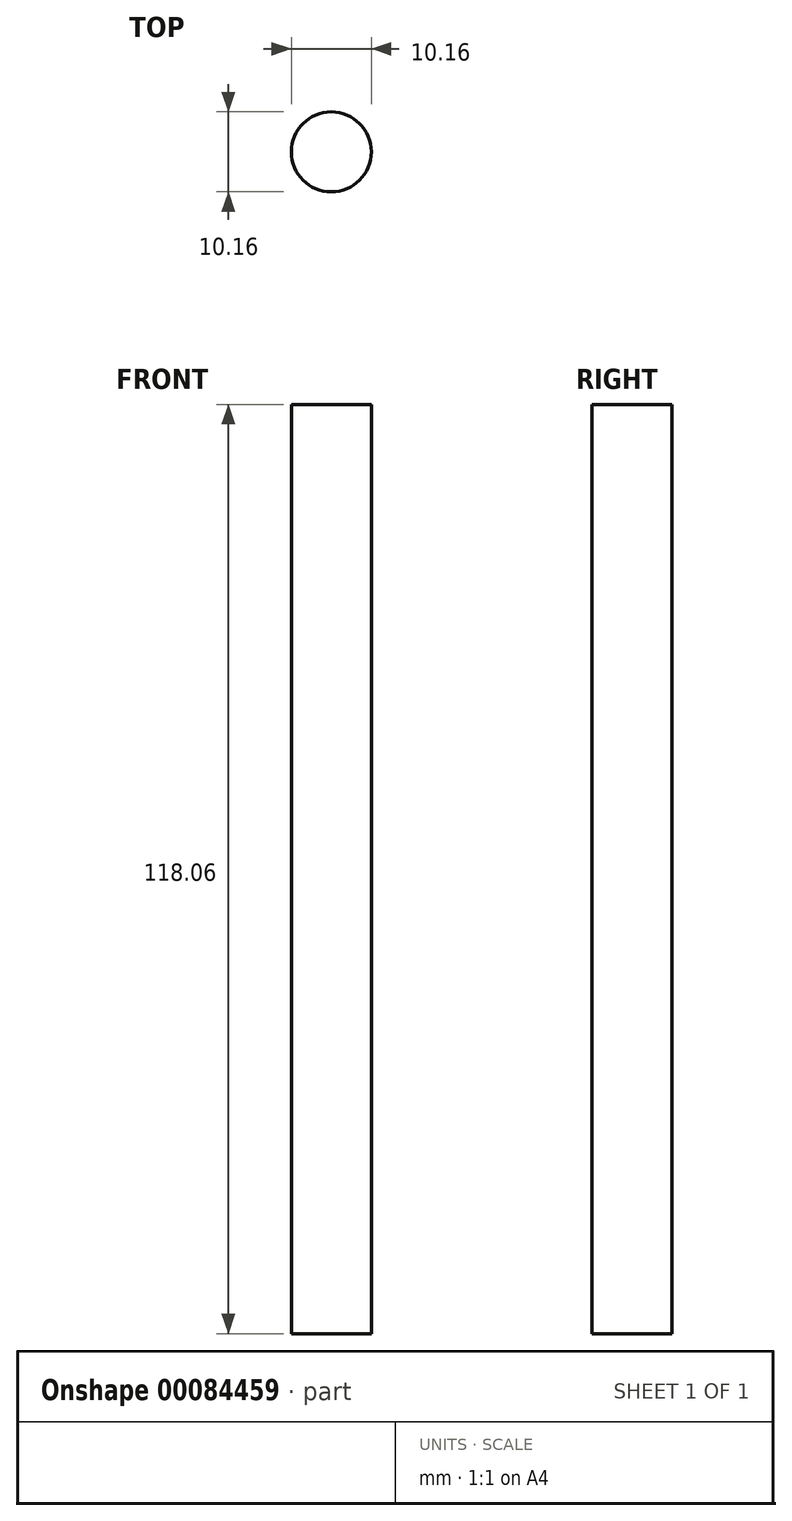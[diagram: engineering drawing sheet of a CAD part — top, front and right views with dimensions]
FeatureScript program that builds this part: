
annotation { "Feature Type Name" : "Feature", "Feature Type Description" : "" }
export const myFeature = defineFeature(function(context is Context, id is Id, definition is map)
    precondition{}
    {
        {
            var Q0;
            Q0=qCreatedBy(makeId("Top.planeOp"),FACE);
            var sketch = newSketch(context, id + "F0", { "sketchPlane" : qUnion([Q0])});
            skCircle(sketch, "E0", {"center": v(0, 0) * mm, "radius": 5.08 * mm});
            skSolve(sketch);
        }
        {
            var Q0;
            Q0=makeQuery(id+"F0.imprint","IMPRINT",FACE,{"disambiguationData":[TD([[makeQuery(id+"F0.imprint","IMPRINT",EDGE,{"derivedFrom":sQuery(id+"F0.wireOp",EDGE,"E0")}),1.0]])]});
            extrude(context, id + "F1", {"entities" : qUnion([Q0]), "depth" : 118.06 * mm});
        }
    });
